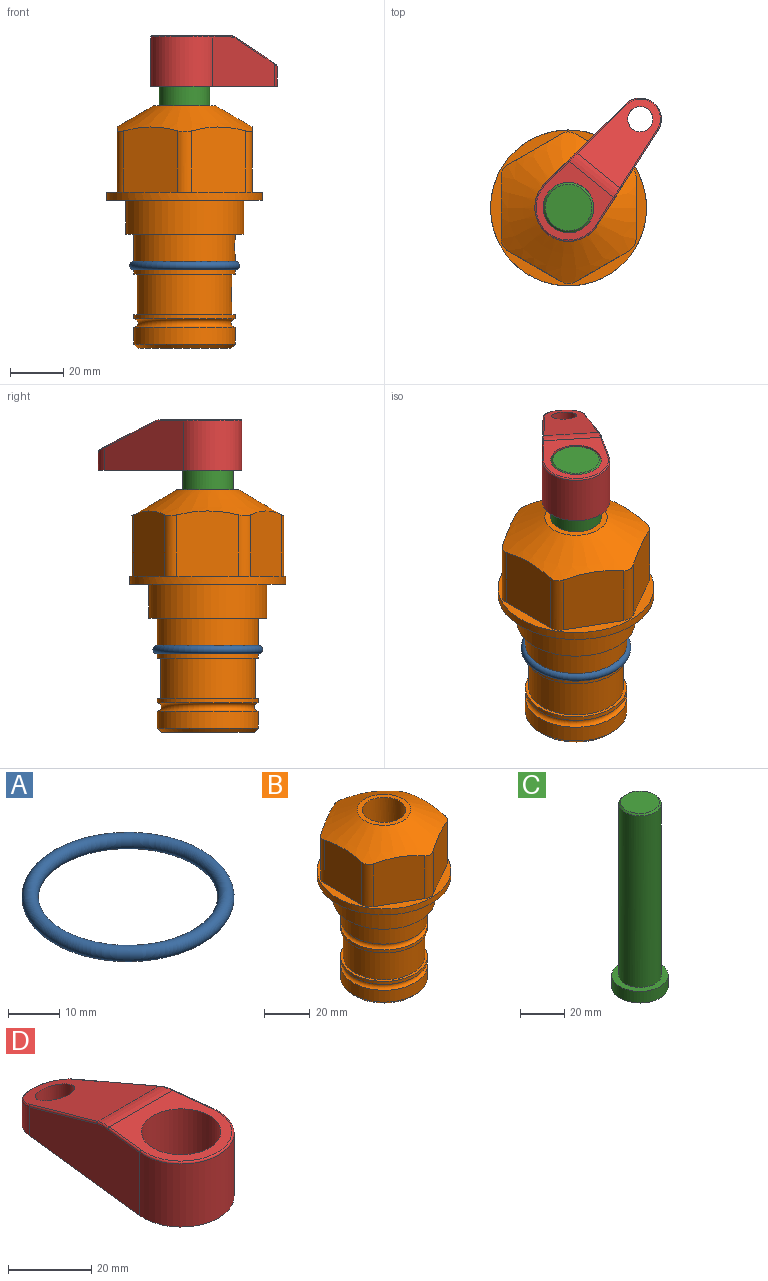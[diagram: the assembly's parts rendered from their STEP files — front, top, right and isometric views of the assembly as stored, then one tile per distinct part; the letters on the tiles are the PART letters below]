
ASSEMBLY  parts=4 mates=2
PART A: 1 faces, bbox 44.7x44.7x3.2 mm
  f0: torus R=19.05mm, axis (0,0,1), area 1193.9mm2
PART B: 36 faces, bbox 58.7x58.7x91.2 mm
  f0: cylinder r=17.78mm len=35.56mm, axis (0,0,1), area 1670.8mm2, adj f23,f24,f31
  f1: cylinder r=19.05mm len=38.1mm, axis (0,0,1), area 1191.9mm2, adj f26,f27,f30
  f2: plane 58.66x58.66mm, normal (0,0,-1), area 1150.6mm2, adj f3,f28
  f3: cylinder r=29.33mm len=58.66mm, axis (0,0,-1), area 585.1mm2, adj f2,f4
  f4: plane 58.66x58.66mm, normal (0,0,1), area 475.9mm2, adj f3,f5,f6,f7,f8,f9,f10,f11
  f5: plane 24.5x20.32mm, normal (-0.5,0.87,0), area 562.8mm2, adj f4,f15,f16,f17
  f6: plane 24.5x20.32mm, normal (0.5,0.87,0), area 562.8mm2, adj f4,f14,f15,f17
  f7: plane 24.5x23.48mm, normal (1,0,0), area 562.8mm2, adj f4,f13,f14,f17
  f8: plane 24.5x20.32mm, normal (0.5,-0.87,0), area 562.8mm2, adj f4,f12,f13,f17
  f9: plane 24.5x20.32mm, normal (-0.5,-0.87,0), area 562.8mm2, adj f4,f11,f12,f17
  f10: plane 24.5x23.48mm, normal (-1,0,0), area 562.8mm2, adj f4,f11,f16,f17
  f11: cylinder r=5.08mm len=23.01mm, axis (0,0,-1), area 121.2mm2, adj f4,f9,f10,f17
  f12: cylinder r=5.08mm len=23.01mm, axis (0,0,-1), area 121.2mm2, adj f4,f8,f9,f17
  f13: cylinder r=5.08mm len=23.01mm, axis (0,0,-1), area 121.2mm2, adj f4,f7,f8,f17
  f14: cylinder r=5.08mm len=23.01mm, axis (0,0,-1), area 121.2mm2, adj f4,f6,f7,f17
  f15: cylinder r=5.08mm len=23.01mm, axis (0,0,-1), area 121.2mm2, adj f4,f5,f6,f17
  f16: cylinder r=5.08mm len=23.01mm, axis (0,0,-1), area 121.2mm2, adj f4,f5,f10,f17
  f17: cone r=11.73mm half-angle=60deg, axis (0,0,-1), area 2071.8mm2, adj f5,f6,f7,f8,f9,f10,f11,f12
  f18: plane 23.46x23.46mm, normal (0,0,1), area 147.4mm2, adj f17,f35
  f19: plane 34.93x34.93mm, normal (0,0,-1), area 958mm2, adj f29
  f20: cylinder r=19.05mm len=38.1mm, axis (0,0,1), area 760.1mm2, adj f21,f29
  f21: torus R=19.05mm, axis (0,0,1), area 565.3mm2, adj f20,f22
  f22: cylinder r=19.05mm len=38.1mm, axis (0,0,1), area 190mm2, adj f21,f23
  f23: plane 38.1x38.1mm, normal (0,0,1), area 146.9mm2, adj f0,f22
  f24: plane 38.1x38.1mm, normal (0,0,-1), area 146.9mm2, adj f0,f25
  f25: cylinder r=19.05mm len=38.1mm, axis (0,0,1), area 190mm2, adj f24,f26
  f26: torus R=19.05mm, axis (0,0,1), area 565.3mm2, adj f1,f25
  f27: plane 44.45x44.45mm, normal (0,0,-1), area 411.7mm2, adj f1,f28
  f28: cylinder r=22.23mm len=44.45mm, axis (0,0,1), area 1773.5mm2, adj f2,f27
  f29: cone r=19.05mm half-angle=45deg, axis (0,0,1), area 257.5mm2, adj f19,f20
  f30: cylinder r=3.17mm len=6.75mm, axis (-1,0,0), area 128mm2, adj f1,f33
  f31: cylinder r=3.17mm len=6.35mm, axis (-1,0,0), area 102.5mm2, adj f0,f33
  f32: plane 25.4x25.4mm, normal (0,0,1), area 506.7mm2, adj f33
  f33: cylinder r=12.7mm len=66.42mm, axis (0,0,-1), area 5236.2mm2, adj f30,f31,f32,f34
  f34: cone r=9.53mm half-angle=30deg, axis (0,0,-1), area 443.4mm2, adj f33,f35
  f35: cylinder r=9.53mm len=19.05mm, axis (0,0,-1), area 849mm2, adj f18,f34
PART C: 6 faces, bbox 25.4x25.4x101.6 mm
  f0: plane 17.46x17.46mm, normal (0,0,1), area 239.5mm2, adj f5
  f1: plane 25.4x25.4mm, normal (0,0,-1), area 506.7mm2, adj f2
  f2: cylinder r=12.7mm len=25.4mm, axis (0,0,1), area 506.7mm2, adj f1,f3
  f3: plane 25.4x25.4mm, normal (0,0,1), area 221.7mm2, adj f2,f4
  f4: cylinder r=9.53mm len=94.46mm, axis (0,0,1), area 5653mm2, adj f3,f5
  f5: cone r=8.73mm half-angle=45deg, axis (0,0,-1), area 64.4mm2, adj f0,f4
PART D: 44 faces, bbox 27.5x64.5x19.1 mm
  f0: plane 2.3x0.95mm, normal (0,0,-1), area 1mm2, adj f25,f30,f34
  f1: plane 63.5x25.4mm, normal (0,0,-1), area 561.7mm2, adj f2,f3,f4,f5,f6,f7,f19,f20
  f2: cylinder r=12.7mm len=25.4mm, axis (0,0,-1), area 792.2mm2, adj f1,f3,f5,f13
  f3: plane 42.33x18.54mm, normal (0.99,0.11,0), area 647mm2, adj f1,f2,f4,f11,f12,f14
  f4: cylinder r=7.94mm len=15.78mm, axis (0,0,-1), area 158.6mm2, adj f1,f3,f5,f16
  f5: plane 42.33x18.54mm, normal (-0.99,0.11,0), area 647mm2, adj f1,f2,f4,f15,f17,f18
  f6: cylinder r=9.53mm len=19.05mm, axis (0,0,-1), area 1140.1mm2, adj f1,f8
  f7: cylinder r=4.76mm len=10.98mm, axis (0,0,-1), area 276.1mm2, adj f1,f9
  f8: plane 25.83x24.38mm, normal (0,0,1), area 262.2mm2, adj f6,f10,f11,f13,f15
  f9: plane 32.49x20.55mm, normal (0,0.34,0.94), area 489.9mm2, adj f7,f10,f14,f16,f18
  f10: cylinder r=12.7mm len=21.49mm, axis (-1,0,0), area 93.2mm2, adj f8,f9,f12,f17
  f11: cylinder r=0.51mm len=12.34mm, axis (0.11,-0.99,0), area 9.9mm2, adj f3,f8,f12,f13
  f12: bspline ~7.62x1.64mm, area 3.5mm2, adj f3,f10,f11,f14
  f13: torus R=12.19mm, axis (0,0,1), area 33.6mm2, adj f2,f8,f11,f15
  f14: cylinder r=0.51mm len=26.01mm, axis (0.1,-0.93,0.34), area 21.6mm2, adj f3,f9,f12,f16
  f15: cylinder r=0.51mm len=12.34mm, axis (0.11,0.99,0), area 9.9mm2, adj f5,f8,f13,f17
  f16: bspline ~15.78x7.05mm, area 15.7mm2, adj f4,f9,f14,f18
  f17: bspline ~7.62x1.64mm, area 3.5mm2, adj f5,f10,f15,f18
  f18: cylinder r=0.51mm len=26.01mm, axis (0.1,0.93,-0.34), area 21.6mm2, adj f5,f9,f16,f17
  f19: plane 21.6x14.29mm, normal (-0.99,-0.11,0), area 242.6mm2, adj f1,f26,f28,f34,f36,f38
  f20: plane 21.6x14.29mm, normal (0.99,-0.11,0), area 242.6mm2, adj f1,f27,f29,f37,f39,f41
  f21: cylinder r=12.7mm len=14.29mm, axis (0,0,-1), area 173.2mm2, adj f1,f26,f27,f30,f31,f33
  f22: cylinder r=7.94mm len=7.63mm, axis (0,0,-1), area 53.8mm2, adj f1,f28,f29,f42
  f23: plane 2.3x0.95mm, normal (0,0,-1), area 1mm2, adj f25,f33,f37
  f24: plane 17.94x12.32mm, normal (0,-0.34,-0.94), area 191.2mm2, adj f25,f38,f41,f42
  f25: cylinder r=9.53mm len=12.93mm, axis (-1,0,0), area 37.5mm2, adj f0,f23,f24,f31,f36,f39
  f26: cylinder r=1.59mm len=14.29mm, axis (0,0,-1), area 49mm2, adj f1,f19,f21,f32
  f27: cylinder r=1.59mm len=14.29mm, axis (0,0,-1), area 49mm2, adj f1,f20,f21,f35
  f28: cylinder r=1.59mm len=7.28mm, axis (0,0,-1), area 22.1mm2, adj f1,f19,f22,f40
  f29: cylinder r=1.59mm len=7.28mm, axis (0,0,-1), area 22.1mm2, adj f1,f20,f22,f43
  f30: torus R=14.29mm, axis (0,0,1), area 5.8mm2, adj f0,f21,f31,f32
  f31: bspline ~11.06x2.73mm, area 20.8mm2, adj f21,f25,f30,f33
  f32: sphere r=1.59mm, area 5.4mm2, adj f26,f30,f34
  f33: torus R=14.29mm, axis (0,0,1), area 5.8mm2, adj f21,f23,f31,f35
  f34: cylinder r=1.59mm len=1.68mm, axis (-0.11,0.99,0), area 2.4mm2, adj f0,f19,f32,f36
  f35: sphere r=1.59mm, area 5.4mm2, adj f27,f33,f37
  f36: bspline ~5.82x2.33mm, area 7.7mm2, adj f19,f25,f34,f38
  f37: cylinder r=1.59mm len=1.68mm, axis (0.11,0.99,0), area 2.4mm2, adj f20,f23,f35,f39
  f38: cylinder r=1.59mm len=18.33mm, axis (0.1,-0.93,0.34), area 46.7mm2, adj f19,f24,f36,f40
  f39: bspline ~5.82x2.33mm, area 7.7mm2, adj f20,f25,f37,f41
  f40: sphere r=1.59mm, area 3.6mm2, adj f28,f38,f42
  f41: cylinder r=1.59mm len=18.33mm, axis (0.1,0.93,-0.34), area 46.7mm2, adj f20,f24,f39,f43
  f42: bspline ~8.31x1.84mm, area 15.3mm2, adj f22,f24,f40,f43
  f43: sphere r=1.59mm, area 3.6mm2, adj f29,f41,f42
PLACE A at identity
PLACE B at identity fixed
PLACE C rot(axis=(0,0,-1),39deg) t=(0,0,-11.64)mm
PLACE D rot(axis=(0,0,-1),39deg) t=(0,0,42.97)mm
MATE cylindrical C.f2 <-> B.f0  axis (0,0,1) through (0,0,14)mm
MATE fastened D.f2 <-> C.f2  axis (0,0,1) through (0,0,62.02)mm
